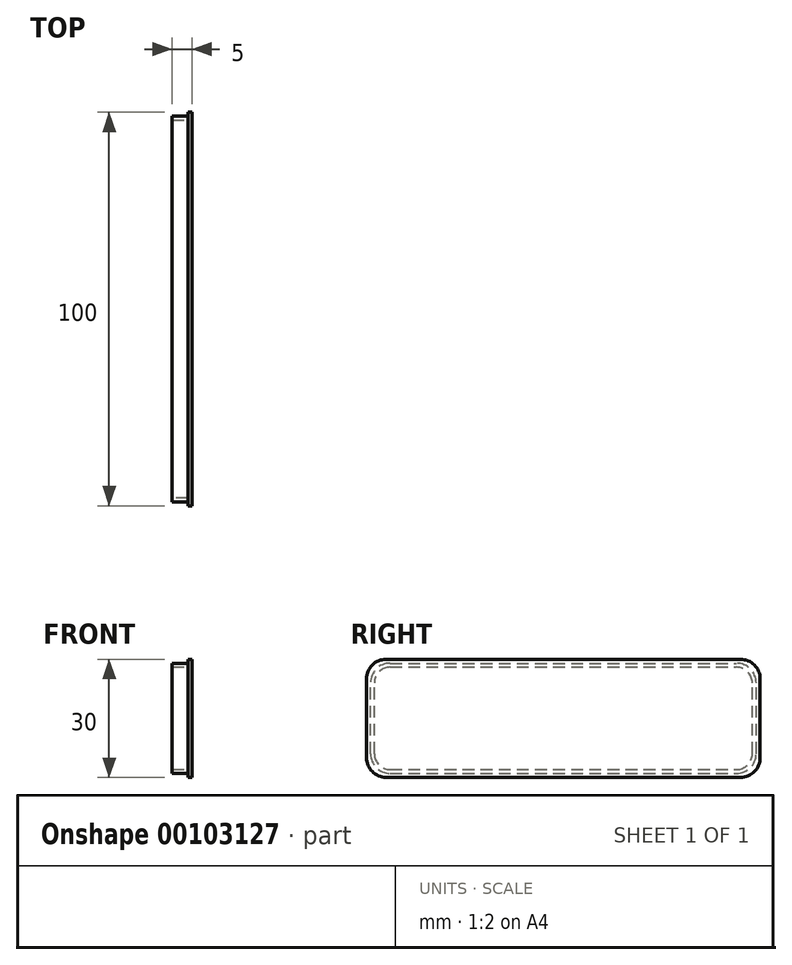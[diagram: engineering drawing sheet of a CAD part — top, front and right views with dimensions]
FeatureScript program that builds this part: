
annotation { "Feature Type Name" : "Feature", "Feature Type Description" : "" }
export const myFeature = defineFeature(function(context is Context, id is Id, definition is map)
    precondition{}
    {
        {
            var Q0;
            Q0=qCreatedBy(makeId("Right.planeOp"),FACE);
            var sketch = newSketch(context, id + "F0", { "sketchPlane" : qUnion([Q0])});
            skLineSegment(sketch, "E0.bottom", {"start": v(-45, -15) * mm, "end": v(45, -15) * mm});
            skLineSegment(sketch, "E0.top", {"start": v(-45, 15) * mm, "end": v(45, 15) * mm});
            skLineSegment(sketch, "E0.left", {"start": v(-50, -10) * mm, "end": v(-50, 10) * mm});
            skLineSegment(sketch, "E0.right", {"start": v(50, -10) * mm, "end": v(50, 10) * mm});
            skPoint(sketch, "E0.middle", {"position": v(0, 0) * mm});
            skPoint(sketch, "E1.visualSharp", {"position": v(50, 15) * mm});
            skArc(sketch, "E1.filletArc", {"start": v(50, 10) * mm, "mid": v(48.54, 13.54) * mm, "end": v(45, 15) * mm});
            skPoint(sketch, "E2.visualSharp", {"position": v(50, -15) * mm});
            skArc(sketch, "E2.filletArc", {"start": v(45, -15) * mm, "mid": v(48.54, -13.54) * mm, "end": v(50, -10) * mm});
            skPoint(sketch, "E3.visualSharp", {"position": v(-50, 15) * mm});
            skArc(sketch, "E3.filletArc", {"start": v(-45, 15) * mm, "mid": v(-48.54, 13.54) * mm, "end": v(-50, 10) * mm});
            skPoint(sketch, "E4.visualSharp", {"position": v(-50, -15) * mm});
            skArc(sketch, "E4.filletArc", {"start": v(-50, -10) * mm, "mid": v(-48.54, -13.54) * mm, "end": v(-45, -15) * mm});
            skSolve(sketch);
        }
        {
            var Q0;
            Q0=makeQuery(id+"F0.imprint","IMPRINT",FACE,{"disambiguationData":[TD([[makeQuery(id+"F0.imprint","IMPRINT",EDGE,{"derivedFrom":sQuery(id+"F0.wireOp",EDGE,"E0.bottom")}),1.0]])]});
            extrude(context, id + "F1", {"entities" : qUnion([Q0]), "depth" : 5 * mm, "offsetDistance" : 25 * mm});
        }
        {
            var Q0;
            Q0=makeQuery(id+"F1.opExtrude","CAP_FACE",FACE,{"disambiguationData":[OSD([sQuery(id+"F0.wireOp",EDGE,"E0.bottom"),sQuery(id+"F0.wireOp",EDGE,"E0.top"),sQuery(id+"F0.wireOp",EDGE,"E0.left"),sQuery(id+"F0.wireOp",EDGE,"E0.right"),sQuery(id+"F0.wireOp",EDGE,"E1.filletArc"),sQuery(id+"F0.wireOp",EDGE,"E2.filletArc"),sQuery(id+"F0.wireOp",EDGE,"E3.filletArc"),sQuery(id+"F0.wireOp",EDGE,"E4.filletArc")])],"isStart":true});
            var sketch = newSketch(context, id + "F2", { "sketchPlane" : qUnion([Q0])});
            skLineSegment(sketch, "E5.bottom", {"start": v(45, -15) * mm, "end": v(-45, -15) * mm});
            skLineSegment(sketch, "E5.top", {"start": v(45, 15) * mm, "end": v(-45, 15) * mm});
            skLineSegment(sketch, "E5.left", {"start": v(50, -10) * mm, "end": v(50, 10) * mm});
            skLineSegment(sketch, "E5.right", {"start": v(-50, -10) * mm, "end": v(-50, 10) * mm});
            skPoint(sketch, "E5.middle", {"position": v(0, 0) * mm});
            skPoint(sketch, "E6.visualSharp", {"position": v(-50, 15) * mm});
            skArc(sketch, "E6.filletArc", {"start": v(-45, 15) * mm, "mid": v(-48.54, 13.54) * mm, "end": v(-50, 10) * mm});
            skPoint(sketch, "E7.visualSharp", {"position": v(-50, -15) * mm});
            skArc(sketch, "E7.filletArc", {"start": v(-50, -10) * mm, "mid": v(-48.54, -13.54) * mm, "end": v(-45, -15) * mm});
            skPoint(sketch, "E8.visualSharp", {"position": v(50, 15) * mm});
            skArc(sketch, "E8.filletArc", {"start": v(50, 10) * mm, "mid": v(48.54, 13.54) * mm, "end": v(45, 15) * mm});
            skPoint(sketch, "E9.visualSharp", {"position": v(50, -15) * mm});
            skArc(sketch, "E9.filletArc", {"start": v(45, -15) * mm, "mid": v(48.54, -13.54) * mm, "end": v(50, -10) * mm});
            skLineSegment(sketch, "E10.bottom", {"start": v(44, -14) * mm, "end": v(-44, -14) * mm});
            skLineSegment(sketch, "E10.top", {"start": v(44, 14) * mm, "end": v(-44, 14) * mm});
            skLineSegment(sketch, "E10.left", {"start": v(49, -9) * mm, "end": v(49, 9) * mm});
            skLineSegment(sketch, "E10.right", {"start": v(-49, -9) * mm, "end": v(-49, 9) * mm});
            skPoint(sketch, "E11.visualSharp", {"position": v(49, 14) * mm});
            skArc(sketch, "E11.filletArc", {"start": v(49, 9) * mm, "mid": v(47.54, 12.54) * mm, "end": v(44, 14) * mm});
            skPoint(sketch, "E12.visualSharp", {"position": v(49, -14) * mm});
            skArc(sketch, "E12.filletArc", {"start": v(44, -14) * mm, "mid": v(47.54, -12.54) * mm, "end": v(49, -9) * mm});
            skPoint(sketch, "E13.visualSharp", {"position": v(-49, -14) * mm});
            skArc(sketch, "E13.filletArc", {"start": v(-49, -9) * mm, "mid": v(-47.54, -12.54) * mm, "end": v(-44, -14) * mm});
            skPoint(sketch, "E14.visualSharp", {"position": v(-49, 14) * mm});
            skArc(sketch, "E14.filletArc", {"start": v(-44, 14) * mm, "mid": v(-47.54, 12.54) * mm, "end": v(-49, 9) * mm});
            skSolve(sketch);
        }
        {
            var Q0;
            Q0=makeQuery(id+"F2.imprint","IMPRINT",FACE,{"disambiguationData":[TD([[makeQuery(id+"F2.imprint","IMPRINT",EDGE,{"derivedFrom":sQuery(id+"F2.wireOp",EDGE,"E5.bottom")}),-1.0]])]});
            extrude(context, id + "F3", {"entities" : qUnion([Q0]), "operationType" : NewBodyOperationType.REMOVE, "oppositeDirection" : true, "depth" : 4 * mm, "offsetDistance" : 25 * mm});
        }
        {
            var Q0;
            Q0=makeQuery(id+"F1.opExtrude","CAP_FACE",FACE,{"disambiguationData":[OSD([sQuery(id+"F0.wireOp",EDGE,"E0.bottom"),sQuery(id+"F0.wireOp",EDGE,"E0.top"),sQuery(id+"F0.wireOp",EDGE,"E0.left"),sQuery(id+"F0.wireOp",EDGE,"E0.right"),sQuery(id+"F0.wireOp",EDGE,"E1.filletArc"),sQuery(id+"F0.wireOp",EDGE,"E2.filletArc"),sQuery(id+"F0.wireOp",EDGE,"E3.filletArc"),sQuery(id+"F0.wireOp",EDGE,"E4.filletArc")])],"isStart":true});
            shell(context, id + "F4", {"entities" : qUnion([Q0]), "thickness" : 1 * mm});
        }
    });
